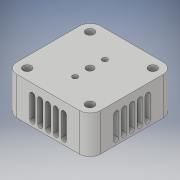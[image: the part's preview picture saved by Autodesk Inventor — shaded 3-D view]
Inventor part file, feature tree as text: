
AUTODESK INVENTOR PART (.ipt)
format: ipt  version: 2018 (Build 220112000, 112)  size: 358,912 bytes
history: native  units: in
note: dims shown in document units (in); Inventor stores cm internally (conversion verified against a paired STEP export)
features: sketch x9, extrude x9, plane x7, projected_geometry x5, pattern_linear x1, mirror x1, fillet x1, pattern_circular x1
ambient origin geometry x8: Origin, YZ Plane, XZ Plane, XY Plane, X Axis, Y Axis, Z Axis, Center Point
bodies: Solid1 (feature_tree)
feature tree (34):
  sketch  "Sketch1"  dims[d0=3.325in d2=2.0in]
  extrude  "Extrusion1"  Depth=2.0in
  sketch  "Sketch4"  dims[d3=2.0in d4=1.802in d5=0.0in]
  sketch  "Sketch7"  dims[d6=0.125in d7=0.125in]
  extrude  "Extrusion13"  Depth=1.802in TaperAngle=0.0deg
  extrude  "Extrusion14"  Depth=0.125in
  extrude  "Extrusion15"  Depth=0.125in
  sketch  "Sketch15"  dims[d12=0.125in d13=0.125in]
  extrude  "Extrusion16"  Depth=0.125in
  extrude  "Extrusion17"  Depth=0.125in
  sketch  "Sketch19"  dims[d14=0.125in d15=0.125in]
  extrude  "Extrusion21"  Depth=0.125in
  pattern_linear  "Rectangular Pattern1"  Spacing1=1.0in  [1 undecoded]
  mirror  "Mirror1"
  sketch  "Sketch21"  dims[d51=1.0in d52=0.0in d53=1.0in d54=0.0in d55=0.375in d56=0.0in d57=0.3438in d58=1.4173in d59=0.7087in d60=0.25in d61=0.5in d62=0.0in d63=0.397in d64=0.5in d65=0.5in d66=0.5in d67=0.5in d68=0.5in d69=0.0in d95=0.25in d96=0.25in d97=1.713in d98=0.0in d99=1.1811in d101=0.375in d102=1.5748in d103=360.0deg d105=0.25in d106=0.0in d107=0.25in d108=0.0in d109=0.5in]
  extrude  "Extrusion22"  Depth=0.25in TaperAngle=0.0deg
  extrude  "Extrusion23"  Depth=0.25in
  fillet  "Fillet2"  Radius=1.4173in
  pattern_circular  "Circular Pattern3"  [2 undecoded]
  projected_geometry  "Projected Loop3"
  sketch  "Sketch13"  dims[d8=0.125in d9=0.125in]
  projected_geometry  "Projected Loop7"
  sketch  "Sketch14"  dims[d10=0.125in d11=0.125in]
  projected_geometry  "Projected Loop8"
  sketch  "Sketch20"  dims[d16=0.25in]
  projected_geometry  "Projected Loop9"
  plane  "Work Plane1"
  plane  "Work Plane2"
  plane  "Work Plane3"
  plane  "Work Plane4"
  plane  "Work Plane5"
  plane  "Work Plane6"
  plane  "Work Plane7"
  projected_geometry  "Projected Loop10"
note: 3 required parameter values undecoded (feature->parameter linkage not recoverable at this tier; creation-order binding heuristic only, values carry confidence <= 0.55)
